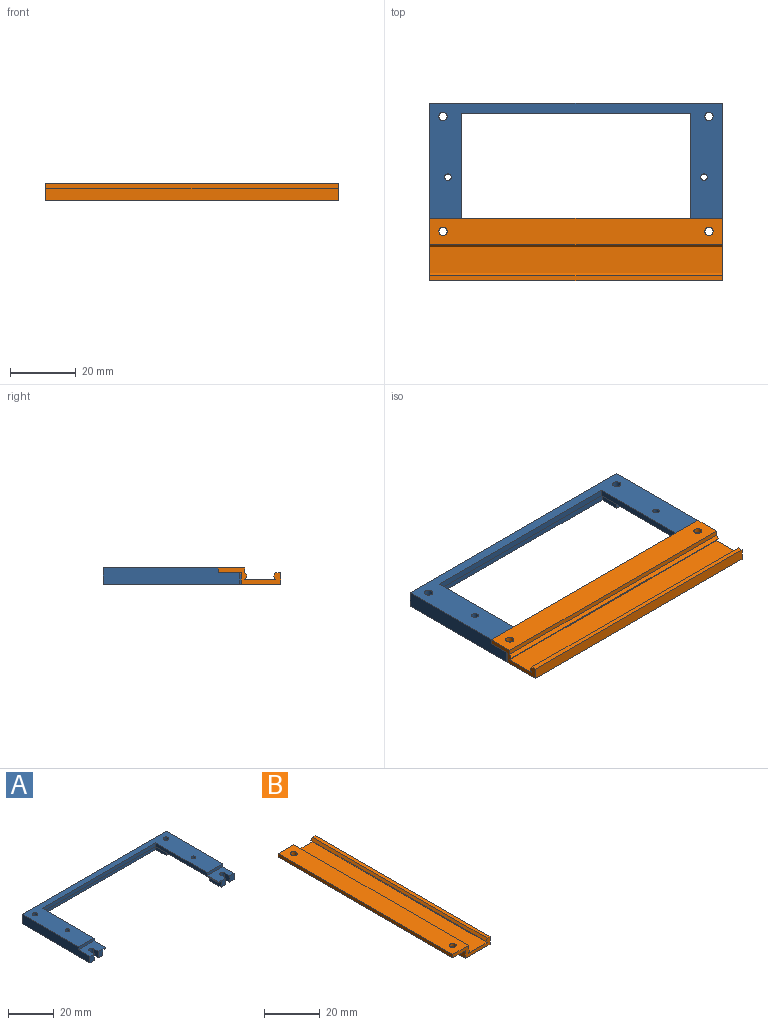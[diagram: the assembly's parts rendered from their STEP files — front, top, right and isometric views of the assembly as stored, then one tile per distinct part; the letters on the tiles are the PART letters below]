
ASSEMBLY  parts=2 mates=1
PART A: 38 faces, bbox 89x42x5 mm
  f0: plane 89x42mm, normal (0,0,-1), area 432.5mm2, adj f3,f4,f5,f6,f7,f9,f10,f11
  f1: plane 9.5x7mm, normal (0,0,1), area 56.5mm2, adj f4,f5,f11,f13,f20,f33,f35,f37
  f2: plane 9.5x7mm, normal (0,0,1), area 56.5mm2, adj f3,f6,f7,f12,f14,f32,f34,f36
  f3: plane 42x5mm, normal (1,0,0), area 199.5mm2, adj f0,f2,f15,f18,f32,f36
  f4: plane 3.5x3mm, normal (-1,0,0), area 10.5mm2, adj f0,f1,f13,f35
  f5: plane 3.5x3mm, normal (1,0,0), area 10.5mm2, adj f0,f1,f13,f37
  f6: plane 3.5x3mm, normal (-1,0,0), area 10.5mm2, adj f0,f2,f14,f36
  f7: plane 3.5x3mm, normal (1,0,0), area 10.5mm2, adj f0,f2,f14,f34
  f8: plane 85.5x40.25mm, normal (0,0,-1), area 539.5mm2, adj f9,f10,f12,f16,f17,f19,f20,f21
  f9: plane 7x3mm, normal (1,0,0), area 21mm2, adj f0,f8,f24,f35
  f10: plane 7x3mm, normal (-1,0,0), area 21mm2, adj f0,f8,f27,f34
  f11: plane 42x5mm, normal (-1,0,0), area 199.5mm2, adj f0,f1,f15,f18,f33,f37
  f12: plane 39x2mm, normal (-1,0,0), area 67.5mm2, adj f2,f8,f15,f19,f32,f34
  f13: cylinder r=1.25mm len=3.5mm, axis (0,0,-1), area 13.7mm2, adj f0,f1,f4,f5
  f14: cylinder r=1.25mm len=3.5mm, axis (0,0,-1), area 13.7mm2, adj f0,f2,f6,f7
  f15: plane 89x35mm, normal (0,0,1), area 858.9mm2, adj f3,f11,f12,f18,f19,f20,f28,f29
  f16: plane 27x3mm, normal (-1,0,0), area 81mm2, adj f0,f8,f26,f27
  f17: plane 73x3mm, normal (0,-1,0), area 219mm2, adj f0,f8,f23,f25
  f18: plane 89x5mm, normal (0,1,0), area 445mm2, adj f0,f3,f11,f15
  f19: plane 70x2mm, normal (0,-1,0), area 140mm2, adj f8,f12,f15,f20
  f20: plane 39x2mm, normal (1,0,0), area 67.5mm2, adj f1,f8,f15,f19,f33,f35
  f21: plane 27x3mm, normal (1,0,0), area 81mm2, adj f0,f8,f22,f24
  f22: plane 6.25x3mm, normal (0,-1,0), area 18.8mm2, adj f0,f8,f21,f23
  f23: plane 6.25x3mm, normal (1,0,0), area 18.8mm2, adj f0,f8,f17,f22
  f24: plane 6.25x3mm, normal (0,1,0), area 18.8mm2, adj f0,f8,f9,f21
  f25: plane 6.25x3mm, normal (-1,0,0), area 18.8mm2, adj f0,f8,f17,f26
  f26: plane 6.25x3mm, normal (0,-1,0), area 18.8mm2, adj f0,f8,f16,f25
  f27: plane 6.25x3mm, normal (0,1,0), area 18.8mm2, adj f0,f8,f10,f16
  f28: cylinder r=1.25mm len=5mm, axis (0,0,-1), area 39.3mm2, adj f0,f15
  f29: cylinder r=1mm len=2mm, axis (0,0,-1), area 12.6mm2, adj f8,f15
  f30: cylinder r=1mm len=2mm, axis (0,0,-1), area 12.6mm2, adj f8,f15
  f31: cylinder r=1.25mm len=5mm, axis (0,0,-1), area 39.3mm2, adj f0,f15
  f32: plane 9.5x1.5mm, normal (0,-1,0), area 14.2mm2, adj f2,f3,f12,f15
  f33: plane 9.5x1.5mm, normal (0,-1,0), area 14.2mm2, adj f1,f11,f15,f20
  f34: plane 4.25x3.5mm, normal (0,-1,0), area 10.4mm2, adj f0,f2,f7,f8,f10,f12
  f35: plane 4.25x3.5mm, normal (0,-1,0), area 10.4mm2, adj f0,f1,f4,f8,f9,f20
  f36: plane 3.5x2.75mm, normal (0,-1,0), area 9.6mm2, adj f0,f2,f3,f6
  f37: plane 3.5x2.75mm, normal (0,-1,0), area 9.6mm2, adj f0,f1,f5,f11
PART B: 17 faces, bbox 19x89x5 mm
  f0: plane 89x6.5mm, normal (0,0,-1), area 568.7mm2, adj f1,f12,f13,f14,f15,f16
  f1: plane 89x3.5mm, normal (-1,0,0), area 311.5mm2, adj f0,f2,f13,f14
  f2: plane 89x12.5mm, normal (0,0,-1), area 1112.5mm2, adj f1,f3,f13,f14
  f3: plane 89x3.5mm, normal (1,0,0), area 311.5mm2, adj f2,f4,f13,f14
  f4: plane 89x1.5mm, normal (0,0,1), area 133.5mm2, adj f3,f5,f13,f14
  f5: plane 89x1mm, normal (-0.8,0,0.6), area 111.3mm2, adj f4,f6,f13,f14
  f6: plane 89x1mm, normal (-0.8,0,-0.6), area 111.3mm2, adj f5,f7,f13,f14
  f7: plane 89x9.5mm, normal (0,0,1), area 845.5mm2, adj f6,f8,f13,f14
  f8: plane 89x1mm, normal (0.8,0,-0.6), area 111.2mm2, adj f7,f9,f13,f14
  f9: plane 89x1mm, normal (0.8,0,0.6), area 111.2mm2, adj f8,f10,f13,f14
  f10: plane 89x1.5mm, normal (1,0,0), area 133.5mm2, adj f9,f11,f13,f14
  f11: plane 89x8mm, normal (0,0,1), area 702.2mm2, adj f10,f12,f13,f14,f15,f16
  f12: plane 89x1.5mm, normal (-1,0,0), area 133.5mm2, adj f0,f11,f13,f14
  f13: plane 19x5mm, normal (0,1,0), area 38.2mm2, adj f0,f1,f2,f3,f4,f5,f6,f7
  f14: plane 19x5mm, normal (0,-1,0), area 38.2mm2, adj f0,f1,f2,f3,f4,f5,f6,f7
  f15: cylinder r=1.25mm len=2.5mm, axis (0,0,1), area 11.8mm2, adj f0,f11
  f16: cylinder r=1.25mm len=2.5mm, axis (0,0,1), area 11.8mm2, adj f0,f11
PLACE A at identity
PLACE B rot(axis=(0,0,-1),90deg) t=(-44.5,-16.5,4.25)mm
MATE fastened B.f15 <-> A.f14  axis (0,0,-1) through (40.5,-16.5,3.5)mm
